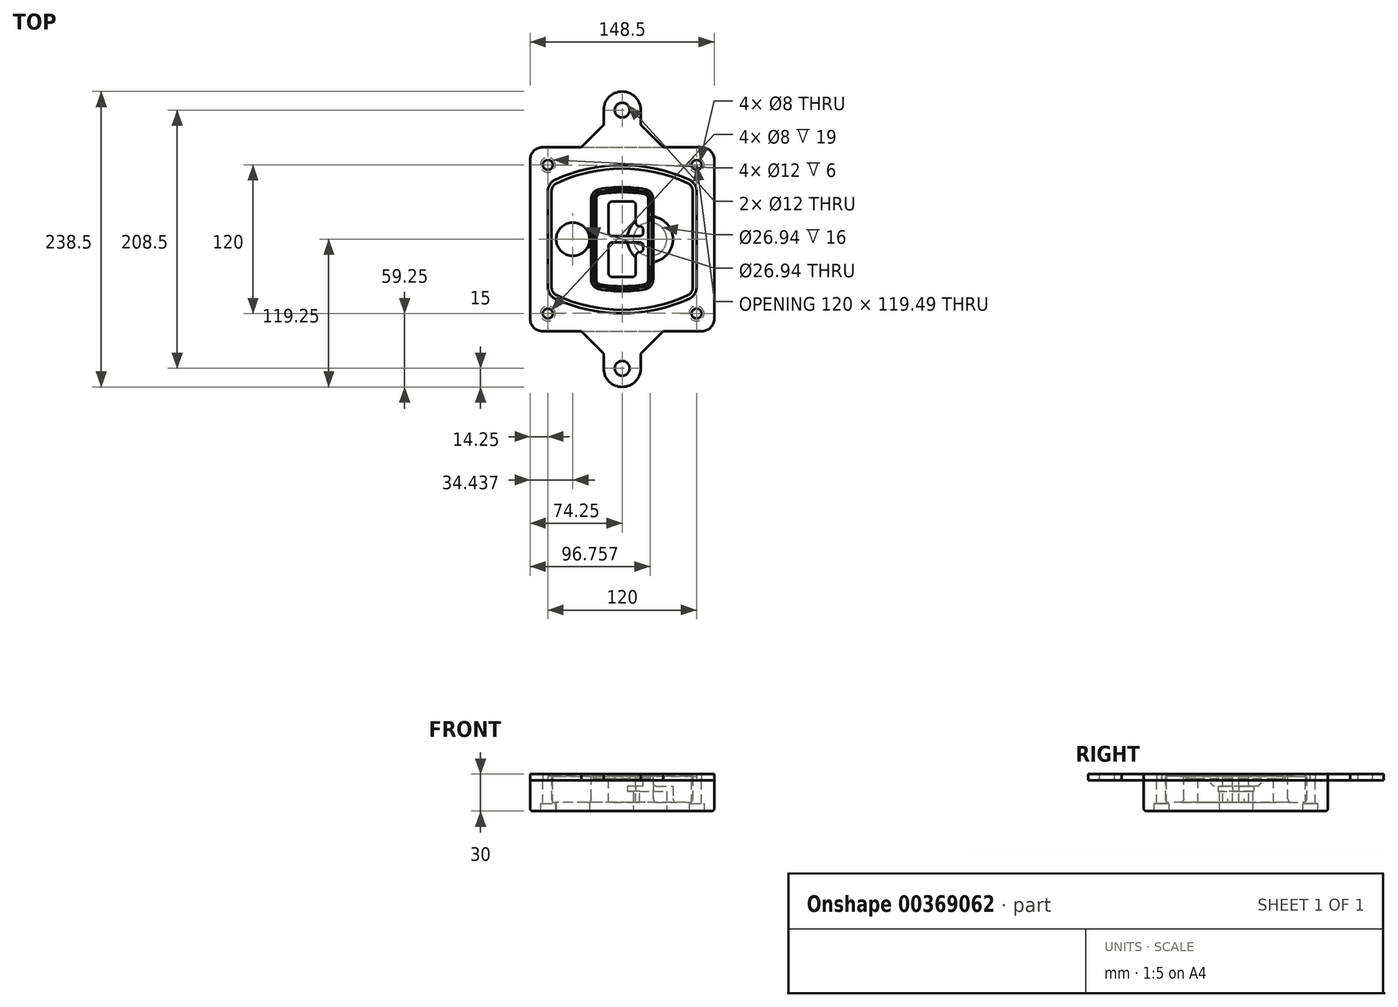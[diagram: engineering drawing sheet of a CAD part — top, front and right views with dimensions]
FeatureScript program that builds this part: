
annotation { "Feature Type Name" : "Feature", "Feature Type Description" : "" }
export const myFeature = defineFeature(function(context is Context, id is Id, definition is map)
    precondition{}
    {
        {
            var Q0;
            Q0=qCreatedBy(makeId("Top.planeOp"),FACE);
            var sketch = newSketch(context, id + "F0", { "sketchPlane" : qUnion([Q0])});
            skPoint(sketch, "E0.rect.middle", {"position": v(0, 0) * mm});
            skLineSegment(sketch, "E1.bottom", {"start": v(-64.25, -74.25) * mm, "end": v(64.25, -74.25) * mm});
            skLineSegment(sketch, "E1.top", {"start": v(-64.25, 74.25) * mm, "end": v(64.25, 74.25) * mm});
            skLineSegment(sketch, "E1.left", {"start": v(-74.25, -64.25) * mm, "end": v(-74.25, 64.25) * mm});
            skLineSegment(sketch, "E1.right", {"start": v(74.25, -64.25) * mm, "end": v(74.25, 64.25) * mm});
            skLineSegment(sketch, "E2", {"start": v(-74.25, 74.25) * mm, "end": v(74.25, -74.25) * mm, "construction": true});
            skLineSegment(sketch, "E3", {"start": v(74.25, 74.25) * mm, "end": v(-74.25, -74.25) * mm, "construction": true});
            skCircle(sketch, "E4", {"center": v(-60, 60) * mm, "radius": 4 * mm});
            skCircle(sketch, "E5", {"center": v(60, 60) * mm, "radius": 4 * mm});
            skCircle(sketch, "E6", {"center": v(60, -60) * mm, "radius": 4 * mm});
            skCircle(sketch, "E7", {"center": v(-60, -60) * mm, "radius": 4 * mm});
            skLineSegment(sketch, "E8", {"start": v(-60, 60) * mm, "end": v(60, 60) * mm, "construction": true});
            skLineSegment(sketch, "E9", {"start": v(60, 60) * mm, "end": v(60, -60) * mm, "construction": true});
            skLineSegment(sketch, "E10", {"start": v(60, -60) * mm, "end": v(-60, -60) * mm, "construction": true});
            skLineSegment(sketch, "E11", {"start": v(-60, -60) * mm, "end": v(-60, 60) * mm, "construction": true});
            skLineSegment(sketch, "E12", {"start": v(-60, 38.83) * mm, "end": v(-60, -38.83) * mm});
            skLineSegment(sketch, "E13", {"start": v(60, 38.83) * mm, "end": v(60, -38.83) * mm});
            skArc(sketch, "E14", {"start": v(54.26, 47.88) * mm, "mid": v(0, 60) * mm, "end": v(-54.26, 47.88) * mm});
            skArc(sketch, "E15", {"start": v(-54.26, -47.88) * mm, "mid": v(0, -60) * mm, "end": v(54.26, -47.88) * mm});
            skLineSegment(sketch, "E16", {"start": v(-60, 0) * mm, "end": v(60, 0) * mm, "construction": true});
            skPoint(sketch, "E17.visualSharp", {"position": v(-60, -45) * mm});
            skArc(sketch, "E17.filletArc", {"start": v(-60, -38.83) * mm, "mid": v(-58.44, -44.2) * mm, "end": v(-54.26, -47.88) * mm});
            skPoint(sketch, "E18.visualSharp", {"position": v(-60, 45) * mm});
            skArc(sketch, "E18.filletArc", {"start": v(-54.26, 47.88) * mm, "mid": v(-58.44, 44.2) * mm, "end": v(-60, 38.83) * mm});
            skPoint(sketch, "E19.visualSharp", {"position": v(60, 45) * mm});
            skArc(sketch, "E19.filletArc", {"start": v(60, 38.83) * mm, "mid": v(58.44, 44.2) * mm, "end": v(54.26, 47.88) * mm});
            skPoint(sketch, "E20.visualSharp", {"position": v(60, -45) * mm});
            skArc(sketch, "E20.filletArc", {"start": v(54.26, -47.88) * mm, "mid": v(58.44, -44.2) * mm, "end": v(60, -38.83) * mm});
            skPoint(sketch, "E21.visualSharp", {"position": v(-74.25, 74.25) * mm});
            skArc(sketch, "E21.filletArc", {"start": v(-64.25, 74.25) * mm, "mid": v(-71.32, 71.32) * mm, "end": v(-74.25, 64.25) * mm});
            skPoint(sketch, "E22.visualSharp", {"position": v(74.25, 74.25) * mm});
            skArc(sketch, "E22.filletArc", {"start": v(74.25, 64.25) * mm, "mid": v(71.32, 71.32) * mm, "end": v(64.25, 74.25) * mm});
            skPoint(sketch, "E23.visualSharp", {"position": v(74.25, -74.25) * mm});
            skArc(sketch, "E23.filletArc", {"start": v(64.25, -74.25) * mm, "mid": v(71.32, -71.32) * mm, "end": v(74.25, -64.25) * mm});
            skPoint(sketch, "E24.visualSharp", {"position": v(-74.25, -74.25) * mm});
            skArc(sketch, "E24.filletArc", {"start": v(-74.25, -64.25) * mm, "mid": v(-71.32, -71.32) * mm, "end": v(-64.25, -74.25) * mm});
            skArc(sketch, "E25.0", {"start": v(57, 38.83) * mm, "mid": v(55.9, 42.58) * mm, "end": v(52.98, 45.17) * mm});
            skLineSegment(sketch, "E25.1", {"start": v(57, 38.83) * mm, "end": v(57, -38.83) * mm});
            skArc(sketch, "E25.2", {"start": v(52.98, -45.17) * mm, "mid": v(55.9, -42.58) * mm, "end": v(57, -38.83) * mm});
            skArc(sketch, "E25.3", {"start": v(-52.98, -45.17) * mm, "mid": v(0, -57) * mm, "end": v(52.98, -45.17) * mm});
            skArc(sketch, "E25.4", {"start": v(-57, -38.83) * mm, "mid": v(-55.9, -42.58) * mm, "end": v(-52.98, -45.17) * mm});
            skArc(sketch, "E25.5", {"start": v(52.98, 45.17) * mm, "mid": v(0, 57) * mm, "end": v(-52.98, 45.17) * mm});
            skLineSegment(sketch, "E25.6", {"start": v(-57, 38.83) * mm, "end": v(-57, -38.83) * mm});
            skArc(sketch, "E25.7", {"start": v(-52.98, 45.17) * mm, "mid": v(-55.9, 42.58) * mm, "end": v(-57, 38.83) * mm});
            skArc(sketch, "E26.0", {"start": v(-55.96, 51.5) * mm, "mid": v(-61.82, 46.33) * mm, "end": v(-64, 38.83) * mm});
            skArc(sketch, "E26.1", {"start": v(55.96, 51.5) * mm, "mid": v(0, 64) * mm, "end": v(-55.96, 51.5) * mm});
            skArc(sketch, "E26.2", {"start": v(64, 38.83) * mm, "mid": v(61.82, 46.33) * mm, "end": v(55.96, 51.5) * mm});
            skLineSegment(sketch, "E26.3", {"start": v(64, 38.83) * mm, "end": v(64, -38.83) * mm});
            skArc(sketch, "E26.4", {"start": v(55.96, -51.5) * mm, "mid": v(61.82, -46.33) * mm, "end": v(64, -38.83) * mm});
            skLineSegment(sketch, "E26.5", {"start": v(-64, 38.83) * mm, "end": v(-64, -38.83) * mm});
            skArc(sketch, "E26.6", {"start": v(-55.96, -51.5) * mm, "mid": v(0, -64) * mm, "end": v(55.96, -51.5) * mm});
            skArc(sketch, "E26.7", {"start": v(-64, -38.83) * mm, "mid": v(-61.82, -46.33) * mm, "end": v(-55.96, -51.5) * mm});
            skSolve(sketch);
        }
        {
            var Q0;
            Q0=makeQuery(id+"F0.imprint","IMPRINT",FACE,{"disambiguationData":[TD([[makeQuery(id+"F0.imprint","IMPRINT",EDGE,{"derivedFrom":sQuery(id+"F0.wireOp",EDGE,"E1.bottom")}),1.0]])]});
            var Q1;
            Q1=makeQuery(id+"F0.imprint","IMPRINT",FACE,{"disambiguationData":[TD([[makeQuery(id+"F0.imprint","IMPRINT",EDGE,{"derivedFrom":sQuery(id+"F0.wireOp",EDGE,"E12")}),1.0]])]});
            var Q2;
            Q2=makeQuery(id+"F0.imprint","IMPRINT",FACE,{"disambiguationData":[TD([[makeQuery(id+"F0.imprint","IMPRINT",EDGE,{"derivedFrom":sQuery(id+"F0.wireOp",EDGE,"E25.0")}),1.0]])]});
            var Q3;
            Q3=makeQuery(id+"F0.imprint","IMPRINT",FACE,{"disambiguationData":[TD([[makeQuery(id+"F0.imprint","IMPRINT",EDGE,{"derivedFrom":sQuery(id+"F0.wireOp",EDGE,"E12")}),-1.0]])]});
            extrude(context, id + "F1", {"entities" : qUnion([Q0, Q1, Q2, Q3]), "oppositeDirection" : true, "depth" : 25 * mm});
        }
        {
            var Q0;
            Q0=makeQuery(id+"F0.imprint","IMPRINT",FACE,{"disambiguationData":[TD([[makeQuery(id+"F0.imprint","IMPRINT",EDGE,{"derivedFrom":sQuery(id+"F0.wireOp",EDGE,"E12")}),1.0]])]});
            extrude(context, id + "F2", {"entities" : qUnion([Q0]), "operationType" : NewBodyOperationType.ADD, "depth" : 3 * mm});
        }
        {
            var Q0;
            Q0=makeQuery(id+"F0.imprint","IMPRINT",FACE,{"disambiguationData":[TD([[makeQuery(id+"F0.imprint","IMPRINT",EDGE,{"derivedFrom":sQuery(id+"F0.wireOp",EDGE,"E25.0")}),1.0]])]});
            extrude(context, id + "F3", {"entities" : qUnion([Q0]), "operationType" : NewBodyOperationType.REMOVE, "oppositeDirection" : true, "depth" : 18 * mm});
        }
        {
            var Q0;
            Q0=makeQuery(id+"F2.opExtrude","CAP_FACE",FACE,{"disambiguationData":[OSD([sQuery(id+"F0.wireOp",EDGE,"E12"),sQuery(id+"F0.wireOp",EDGE,"E13"),sQuery(id+"F0.wireOp",EDGE,"E14"),sQuery(id+"F0.wireOp",EDGE,"E15"),sQuery(id+"F0.wireOp",EDGE,"E17.filletArc"),sQuery(id+"F0.wireOp",EDGE,"E18.filletArc"),sQuery(id+"F0.wireOp",EDGE,"E19.filletArc"),sQuery(id+"F0.wireOp",EDGE,"E20.filletArc"),sQuery(id+"F0.wireOp",EDGE,"E25.0"),sQuery(id+"F0.wireOp",EDGE,"E25.1"),sQuery(id+"F0.wireOp",EDGE,"E25.2"),sQuery(id+"F0.wireOp",EDGE,"E25.3"),sQuery(id+"F0.wireOp",EDGE,"E25.4"),sQuery(id+"F0.wireOp",EDGE,"E25.5"),sQuery(id+"F0.wireOp",EDGE,"E25.6"),sQuery(id+"F0.wireOp",EDGE,"E25.7")])],"isStart":false});
            var sketch = newSketch(context, id + "F4", { "sketchPlane" : qUnion([Q0])});
            skArc(sketch, "E27.0", {"start": v(-18.34, -40.45) * mm, "mid": v(0, -42) * mm, "end": v(18.34, -40.45) * mm});
            skArc(sketch, "E28.0", {"start": v(18.34, 40.45) * mm, "mid": v(0, 42) * mm, "end": v(-18.34, 40.45) * mm});
            skLineSegment(sketch, "E29", {"start": v(-25, 32.57) * mm, "end": v(-25, -32.57) * mm});
            skLineSegment(sketch, "E30", {"start": v(25, 32.57) * mm, "end": v(25, -32.57) * mm});
            skLineSegment(sketch, "E31", {"start": v(-25, 39.1) * mm, "end": v(25, 39.1) * mm, "construction": true});
            skLineSegment(sketch, "E32", {"start": v(-25, -39.1) * mm, "end": v(25, -39.1) * mm, "construction": true});
            skPoint(sketch, "E33.visualSharp", {"position": v(-25, 39.1) * mm});
            skArc(sketch, "E33.filletArc", {"start": v(-18.34, 40.45) * mm, "mid": v(-23.11, 37.73) * mm, "end": v(-25, 32.57) * mm});
            skPoint(sketch, "E34.visualSharp", {"position": v(25, 39.1) * mm});
            skArc(sketch, "E34.filletArc", {"start": v(25, 32.57) * mm, "mid": v(23.11, 37.73) * mm, "end": v(18.34, 40.45) * mm});
            skPoint(sketch, "E35.visualSharp", {"position": v(25, -39.1) * mm});
            skArc(sketch, "E35.filletArc", {"start": v(18.34, -40.45) * mm, "mid": v(23.11, -37.73) * mm, "end": v(25, -32.57) * mm});
            skPoint(sketch, "E36.visualSharp", {"position": v(-25, -39.1) * mm});
            skArc(sketch, "E36.filletArc", {"start": v(-25, -32.57) * mm, "mid": v(-23.11, -37.73) * mm, "end": v(-18.34, -40.45) * mm});
            skArc(sketch, "E37.0", {"start": v(52.98, 45.17) * mm, "mid": v(0, 57) * mm, "end": v(-52.98, 45.17) * mm});
            skArc(sketch, "E37.1", {"start": v(-52.98, 45.17) * mm, "mid": v(-55.9, 42.58) * mm, "end": v(-57, 38.83) * mm});
            skLineSegment(sketch, "E37.2", {"start": v(-57, 38.83) * mm, "end": v(-57, -38.83) * mm});
            skArc(sketch, "E37.3", {"start": v(-57, -38.83) * mm, "mid": v(-55.9, -42.58) * mm, "end": v(-52.98, -45.17) * mm});
            skArc(sketch, "E37.4", {"start": v(-52.98, -45.17) * mm, "mid": v(0, -57) * mm, "end": v(52.98, -45.17) * mm});
            skArc(sketch, "E37.5", {"start": v(52.98, -45.17) * mm, "mid": v(55.9, -42.58) * mm, "end": v(57, -38.83) * mm});
            skLineSegment(sketch, "E37.6", {"start": v(57, 38.83) * mm, "end": v(57, -38.83) * mm});
            skArc(sketch, "E37.7", {"start": v(57, 38.83) * mm, "mid": v(55.9, 42.58) * mm, "end": v(52.98, 45.17) * mm});
            skLineSegment(sketch, "E38.0", {"start": v(23, 32.57) * mm, "end": v(23, -32.57) * mm});
            skArc(sketch, "E38.1", {"start": v(18, -38.48) * mm, "mid": v(21.58, -36.44) * mm, "end": v(23, -32.57) * mm});
            skArc(sketch, "E38.2", {"start": v(-18, -38.48) * mm, "mid": v(0, -40) * mm, "end": v(18, -38.48) * mm});
            skArc(sketch, "E38.3", {"start": v(-23, -32.57) * mm, "mid": v(-21.58, -36.44) * mm, "end": v(-18, -38.48) * mm});
            skLineSegment(sketch, "E38.4", {"start": v(-23, 32.57) * mm, "end": v(-23, -32.57) * mm});
            skArc(sketch, "E38.5", {"start": v(23, 32.57) * mm, "mid": v(21.58, 36.44) * mm, "end": v(18, 38.48) * mm});
            skArc(sketch, "E38.6", {"start": v(-18, 38.48) * mm, "mid": v(-21.58, 36.44) * mm, "end": v(-23, 32.57) * mm});
            skArc(sketch, "E38.7", {"start": v(18, 38.48) * mm, "mid": v(0, 40) * mm, "end": v(-18, 38.48) * mm});
            skArc(sketch, "E39.0", {"start": v(21, 32.57) * mm, "mid": v(20.06, 35.15) * mm, "end": v(17.67, 36.5) * mm});
            skLineSegment(sketch, "E39.1", {"start": v(21, 32.57) * mm, "end": v(21, -32.57) * mm});
            skArc(sketch, "E39.2", {"start": v(17.67, -36.5) * mm, "mid": v(20.06, -35.15) * mm, "end": v(21, -32.57) * mm});
            skArc(sketch, "E39.3", {"start": v(-17.67, -36.5) * mm, "mid": v(0, -38) * mm, "end": v(17.67, -36.5) * mm});
            skArc(sketch, "E39.4", {"start": v(-21, -32.57) * mm, "mid": v(-20.06, -35.15) * mm, "end": v(-17.67, -36.5) * mm});
            skArc(sketch, "E39.5", {"start": v(17.67, 36.5) * mm, "mid": v(0, 38) * mm, "end": v(-17.67, 36.5) * mm});
            skLineSegment(sketch, "E39.6", {"start": v(-21, 32.57) * mm, "end": v(-21, -32.57) * mm});
            skArc(sketch, "E39.7", {"start": v(-17.67, 36.5) * mm, "mid": v(-20.06, 35.15) * mm, "end": v(-21, 32.57) * mm});
            skLineSegment(sketch, "E40", {"start": v(-25, 0) * mm, "end": v(25, 0) * mm, "construction": true});
            skLineSegment(sketch, "E41", {"start": v(-11, 5.5) * mm, "end": v(-11, 27.5) * mm});
            skLineSegment(sketch, "E42", {"start": v(-8, 30.5) * mm, "end": v(8, 30.5) * mm});
            skLineSegment(sketch, "E43", {"start": v(11, 27.5) * mm, "end": v(11, 13.5) * mm});
            skLineSegment(sketch, "E44", {"start": v(14, 10.5) * mm, "end": v(14, 10.5) * mm});
            skLineSegment(sketch, "E45", {"start": v(17, 7.5) * mm, "end": v(17, 5.5) * mm});
            skLineSegment(sketch, "E46", {"start": v(14, 2.5) * mm, "end": v(-8, 2.5) * mm});
            skPoint(sketch, "E47.visualSharp", {"position": v(-11, 30.5) * mm});
            skArc(sketch, "E47.filletArc", {"start": v(-8, 30.5) * mm, "mid": v(-10.12, 29.62) * mm, "end": v(-11, 27.5) * mm});
            skPoint(sketch, "E48.visualSharp", {"position": v(11, 30.5) * mm});
            skArc(sketch, "E48.filletArc", {"start": v(11, 27.5) * mm, "mid": v(10.12, 29.62) * mm, "end": v(8, 30.5) * mm});
            skPoint(sketch, "E49.visualSharp", {"position": v(11, 10.5) * mm});
            skArc(sketch, "E49.filletArc", {"start": v(11, 13.5) * mm, "mid": v(11.88, 11.38) * mm, "end": v(14, 10.5) * mm});
            skPoint(sketch, "E50.visualSharp", {"position": v(17, 10.5) * mm});
            skArc(sketch, "E50.filletArc", {"start": v(17, 7.5) * mm, "mid": v(16.12, 9.62) * mm, "end": v(14, 10.5) * mm});
            skPoint(sketch, "E51.visualSharp", {"position": v(17, 2.5) * mm});
            skArc(sketch, "E51.filletArc", {"start": v(14, 2.5) * mm, "mid": v(16.12, 3.38) * mm, "end": v(17, 5.5) * mm});
            skPoint(sketch, "E52.visualSharp", {"position": v(-11, 2.5) * mm});
            skArc(sketch, "E52.filletArc", {"start": v(-11, 5.5) * mm, "mid": v(-10.12, 3.38) * mm, "end": v(-8, 2.5) * mm});
            skLineSegment(sketch, "E53.0.MirrorCS", {"start": v(14, -2.5) * mm, "end": v(-8, -2.5) * mm});
            skArc(sketch, "E54.0.MirrorCS", {"start": v(-11, -5.5) * mm, "mid": v(-10.12, -3.38) * mm, "end": v(-8, -2.5) * mm});
            skLineSegment(sketch, "E55.0.MirrorCS", {"start": v(-11, -5.5) * mm, "end": v(-11, -27.5) * mm});
            skArc(sketch, "E56.0.MirrorCS", {"start": v(-8, -30.5) * mm, "mid": v(-10.12, -29.62) * mm, "end": v(-11, -27.5) * mm});
            skLineSegment(sketch, "E57.0.MirrorCS", {"start": v(-8, -30.5) * mm, "end": v(8, -30.5) * mm});
            skArc(sketch, "E58.0.MirrorCS", {"start": v(11, -27.5) * mm, "mid": v(10.12, -29.62) * mm, "end": v(8, -30.5) * mm});
            skLineSegment(sketch, "E59.0.MirrorCS", {"start": v(11, -27.5) * mm, "end": v(11, -13.5) * mm});
            skArc(sketch, "E60.0.MirrorCS", {"start": v(11, -13.5) * mm, "mid": v(11.88, -11.38) * mm, "end": v(14, -10.5) * mm});
            skArc(sketch, "E61.0.MirrorCS", {"start": v(17, -7.5) * mm, "mid": v(16.12, -9.62) * mm, "end": v(14, -10.5) * mm});
            skLineSegment(sketch, "E62.0.MirrorCS", {"start": v(17, -7.5) * mm, "end": v(17, -5.5) * mm});
            skArc(sketch, "E63.0.MirrorCS", {"start": v(14, -2.5) * mm, "mid": v(16.12, -3.38) * mm, "end": v(17, -5.5) * mm});
            skSolve(sketch);
        }
        {
            var Q0;
            Q0=makeQuery(id+"F4.imprint","IMPRINT",FACE,{"disambiguationData":[TD([[makeQuery(id+"F4.imprint","IMPRINT",EDGE,{"derivedFrom":sQuery(id+"F4.wireOp",EDGE,"E27.0")}),1.0]])]});
            var Q1;
            Q1=makeQuery(id+"F4.imprint","IMPRINT",FACE,{"disambiguationData":[TD([[makeQuery(id+"F4.imprint","IMPRINT",EDGE,{"derivedFrom":sQuery(id+"F4.wireOp",EDGE,"E38.0")}),-1.0]])]});
            var Q2;
            Q2=makeQuery(id+"F4.imprint","IMPRINT",FACE,{"disambiguationData":[TD([[makeQuery(id+"F4.imprint","IMPRINT",EDGE,{"derivedFrom":sQuery(id+"F4.wireOp",EDGE,"E39.0")}),1.0]])]});
            extrude(context, id + "F5", {"entities" : qUnion([Q0, Q1, Q2]), "operationType" : NewBodyOperationType.ADD, "endBound" : BoundingType.UP_TO_NEXT, "oppositeDirection" : true, "depth" : 25 * mm});
        }
        {
            var Q0;
            Q0=makeQuery(id+"F4.imprint","IMPRINT",FACE,{"disambiguationData":[TD([[makeQuery(id+"F4.imprint","IMPRINT",EDGE,{"derivedFrom":sQuery(id+"F4.wireOp",EDGE,"E38.0")}),-1.0]])]});
            extrude(context, id + "F6", {"entities" : qUnion([Q0]), "operationType" : NewBodyOperationType.REMOVE, "oppositeDirection" : true, "depth" : 2 * mm});
        }
        {
            var Q0;
            Q0=makeQuery(id+"F1.opExtrude","CAP_FACE",FACE,{"disambiguationData":[OSD([sQuery(id+"F0.wireOp",EDGE,"E1.bottom"),sQuery(id+"F0.wireOp",EDGE,"E1.top"),sQuery(id+"F0.wireOp",EDGE,"E1.left"),sQuery(id+"F0.wireOp",EDGE,"E1.right"),sQuery(id+"F0.wireOp",EDGE,"E4"),sQuery(id+"F0.wireOp",EDGE,"E5"),sQuery(id+"F0.wireOp",EDGE,"E6"),sQuery(id+"F0.wireOp",EDGE,"E7"),sQuery(id+"F0.wireOp",EDGE,"E21.filletArc"),sQuery(id+"F0.wireOp",EDGE,"E22.filletArc"),sQuery(id+"F0.wireOp",EDGE,"E23.filletArc"),sQuery(id+"F0.wireOp",EDGE,"E24.filletArc")])],"isStart":false});
            var sketch = newSketch(context, id + "F7", { "sketchPlane" : qUnion([Q0])});
            skCircle(sketch, "E64", {"center": v(22.5, 0) * mm, "radius": 13.47 * mm});
            skCircle(sketch, "E65", {"center": v(-39.81, 0) * mm, "radius": 13.47 * mm});
            skLineSegment(sketch, "E66", {"start": v(74.25, 0) * mm, "end": v(-74.25, 0) * mm});
            skCircle(sketch, "E67", {"center": v(22.5, 0) * mm, "radius": 18.47 * mm});
            skCircle(sketch, "E68", {"center": v(60, -60) * mm, "radius": 6 * mm});
            skCircle(sketch, "E69", {"center": v(-60, -60) * mm, "radius": 6 * mm});
            skCircle(sketch, "E70", {"center": v(-60, 60) * mm, "radius": 6 * mm});
            skCircle(sketch, "E71", {"center": v(60, 60) * mm, "radius": 6 * mm});
            skSolve(sketch);
        }
        {
            var Q0;
            {var subQ1=sQuery(id+"F7.wireOp",EDGE,"E66");var subQ4=sQuery(id+"F7.wireOp",EDGE,"E64");var subQ6=makeQuery(id+"F7.imprint","INTERSECT",VERTEX,{"disambiguationData":[OD(0.0)],"derivedFrom":[subQ4,subQ1]});Q0=makeQuery(id+"F7.imprint","IMPRINT",FACE,{"disambiguationData":[TD([[makeQuery(id+"F7.imprint","IMPRINT",EDGE,{"disambiguationData":[TD([[subQ6,-1.0]])],"derivedFrom":subQ4}),-1.0]])]});}
            var Q1;
            {var subQ0=sQuery(id+"F7.wireOp",EDGE,"E66");var subQ1=sQuery(id+"F7.wireOp",EDGE,"E64");var subQ3=makeQuery(id+"F7.imprint","INTERSECT",VERTEX,{"disambiguationData":[OD(0.0)],"derivedFrom":[subQ1,subQ0]});Q1=makeQuery(id+"F7.imprint","IMPRINT",FACE,{"disambiguationData":[TD([[makeQuery(id+"F7.imprint","IMPRINT",EDGE,{"disambiguationData":[TD([[subQ3,-1.0]])],"derivedFrom":subQ1}),1.0]])]});}
            var Q2;
            {var subQ0=sQuery(id+"F7.wireOp",EDGE,"E66");var subQ1=sQuery(id+"F7.wireOp",EDGE,"E64");var subQ3=makeQuery(id+"F7.imprint","INTERSECT",VERTEX,{"disambiguationData":[OD(0.0)],"derivedFrom":[subQ1,subQ0]});Q2=makeQuery(id+"F7.imprint","IMPRINT",FACE,{"disambiguationData":[TD([[makeQuery(id+"F7.imprint","IMPRINT",EDGE,{"disambiguationData":[TD([[subQ3,1.0]])],"derivedFrom":subQ1}),1.0]])]});}
            var Q3;
            {var subQ1=sQuery(id+"F7.wireOp",EDGE,"E66");var subQ4=sQuery(id+"F7.wireOp",EDGE,"E64");var subQ6=makeQuery(id+"F7.imprint","INTERSECT",VERTEX,{"disambiguationData":[OD(0.0)],"derivedFrom":[subQ4,subQ1]});Q3=makeQuery(id+"F7.imprint","IMPRINT",FACE,{"disambiguationData":[TD([[makeQuery(id+"F7.imprint","IMPRINT",EDGE,{"disambiguationData":[TD([[subQ6,1.0]])],"derivedFrom":subQ4}),-1.0]])]});}
            extrude(context, id + "F8", {"entities" : qUnion([Q0, Q1, Q2, Q3]), "operationType" : NewBodyOperationType.ADD, "oppositeDirection" : true, "depth" : 20 * mm});
        }
        {
            var Q0;
            {var subQ0=sQuery(id+"F7.wireOp",EDGE,"E66");var subQ1=sQuery(id+"F7.wireOp",EDGE,"E64");var subQ3=makeQuery(id+"F7.imprint","INTERSECT",VERTEX,{"disambiguationData":[OD(0.0)],"derivedFrom":[subQ1,subQ0]});Q0=makeQuery(id+"F7.imprint","IMPRINT",FACE,{"disambiguationData":[TD([[makeQuery(id+"F7.imprint","IMPRINT",EDGE,{"disambiguationData":[TD([[subQ3,-1.0]])],"derivedFrom":subQ1}),1.0]])]});}
            var Q1;
            {var subQ0=sQuery(id+"F7.wireOp",EDGE,"E66");var subQ1=sQuery(id+"F7.wireOp",EDGE,"E64");var subQ3=makeQuery(id+"F7.imprint","INTERSECT",VERTEX,{"disambiguationData":[OD(0.0)],"derivedFrom":[subQ1,subQ0]});Q1=makeQuery(id+"F7.imprint","IMPRINT",FACE,{"disambiguationData":[TD([[makeQuery(id+"F7.imprint","IMPRINT",EDGE,{"disambiguationData":[TD([[subQ3,1.0]])],"derivedFrom":subQ1}),1.0]])]});}
            extrude(context, id + "F9", {"entities" : qUnion([Q0, Q1]), "operationType" : NewBodyOperationType.REMOVE, "oppositeDirection" : true, "depth" : 16 * mm});
        }
        {
            var Q0;
            {var subQ0=sQuery(id+"F7.wireOp",EDGE,"E66");var subQ1=sQuery(id+"F7.wireOp",EDGE,"E65");var subQ3=makeQuery(id+"F7.imprint","INTERSECT",VERTEX,{"disambiguationData":[OD(0.0)],"derivedFrom":[subQ1,subQ0]});Q0=makeQuery(id+"F7.imprint","IMPRINT",FACE,{"disambiguationData":[TD([[makeQuery(id+"F7.imprint","IMPRINT",EDGE,{"disambiguationData":[TD([[subQ3,-1.0]])],"derivedFrom":subQ1}),1.0]])]});}
            var Q1;
            {var subQ0=sQuery(id+"F7.wireOp",EDGE,"E66");var subQ1=sQuery(id+"F7.wireOp",EDGE,"E65");var subQ3=makeQuery(id+"F7.imprint","INTERSECT",VERTEX,{"disambiguationData":[OD(0.0)],"derivedFrom":[subQ1,subQ0]});Q1=makeQuery(id+"F7.imprint","IMPRINT",FACE,{"disambiguationData":[TD([[makeQuery(id+"F7.imprint","IMPRINT",EDGE,{"disambiguationData":[TD([[subQ3,1.0]])],"derivedFrom":subQ1}),1.0]])]});}
            extrude(context, id + "F10", {"entities" : qUnion([Q0, Q1]), "operationType" : NewBodyOperationType.REMOVE, "oppositeDirection" : true, "depth" : 25 * mm});
        }
        {
            var Q0;
            Q0=makeQuery(id+"F7.imprint","IMPRINT",FACE,{"disambiguationData":[TD([[makeQuery(id+"F7.imprint","IMPRINT",EDGE,{"derivedFrom":sQuery(id+"F7.wireOp",EDGE,"E68")}),1.0]])]});
            var Q1;
            Q1=makeQuery(id+"F7.imprint","IMPRINT",FACE,{"disambiguationData":[TD([[makeQuery(id+"F7.imprint","IMPRINT",EDGE,{"derivedFrom":makeQuery(id+"F1.opExtrude","CAP_EDGE",EDGE,{"disambiguationData":[OSD([sQuery(id+"F0.wireOp",EDGE,"E5")])],"isStart":false})}),-1.0]])]});
            var Q2;
            Q2=makeQuery(id+"F7.imprint","IMPRINT",FACE,{"disambiguationData":[TD([[makeQuery(id+"F7.imprint","IMPRINT",EDGE,{"derivedFrom":sQuery(id+"F7.wireOp",EDGE,"E69")}),1.0]])]});
            var Q3;
            Q3=makeQuery(id+"F7.imprint","IMPRINT",FACE,{"disambiguationData":[TD([[makeQuery(id+"F7.imprint","IMPRINT",EDGE,{"derivedFrom":makeQuery(id+"F1.opExtrude","CAP_EDGE",EDGE,{"disambiguationData":[OSD([sQuery(id+"F0.wireOp",EDGE,"E4")])],"isStart":false})}),-1.0]])]});
            var Q4;
            Q4=makeQuery(id+"F7.imprint","IMPRINT",FACE,{"disambiguationData":[TD([[makeQuery(id+"F7.imprint","IMPRINT",EDGE,{"derivedFrom":sQuery(id+"F7.wireOp",EDGE,"E70")}),1.0]])]});
            var Q5;
            Q5=makeQuery(id+"F7.imprint","IMPRINT",FACE,{"disambiguationData":[TD([[makeQuery(id+"F7.imprint","IMPRINT",EDGE,{"derivedFrom":makeQuery(id+"F1.opExtrude","CAP_EDGE",EDGE,{"disambiguationData":[OSD([sQuery(id+"F0.wireOp",EDGE,"E7")])],"isStart":false})}),-1.0]])]});
            var Q6;
            Q6=makeQuery(id+"F7.imprint","IMPRINT",FACE,{"disambiguationData":[TD([[makeQuery(id+"F7.imprint","IMPRINT",EDGE,{"derivedFrom":sQuery(id+"F7.wireOp",EDGE,"E71")}),1.0]])]});
            var Q7;
            Q7=makeQuery(id+"F7.imprint","IMPRINT",FACE,{"disambiguationData":[TD([[makeQuery(id+"F7.imprint","IMPRINT",EDGE,{"derivedFrom":makeQuery(id+"F1.opExtrude","CAP_EDGE",EDGE,{"disambiguationData":[OSD([sQuery(id+"F0.wireOp",EDGE,"E6")])],"isStart":false})}),-1.0]])]});
            extrude(context, id + "F11", {"entities" : qUnion([Q0, Q1, Q2, Q3, Q4, Q5, Q6, Q7]), "operationType" : NewBodyOperationType.REMOVE, "oppositeDirection" : true, "depth" : 6 * mm});
        }
        {
            var Q0;
            Q0=makeQuery(id+"F9.boolean.opBoolean","COPY",FACE,{"derivedFrom":makeQuery(id+"F9.opExtrude","CAP_FACE",FACE,{"disambiguationData":[OSD([sQuery(id+"F7.wireOp",EDGE,"E64")])],"isStart":false})});
            var sketch = newSketch(context, id + "F12", { "sketchPlane" : qUnion([Q0])});
            skArc(sketch, "E72.0", {"start": v(11, 14.45) * mm, "mid": v(6.45, 9.13) * mm, "end": v(4.2, 2.5) * mm});
            skArc(sketch, "E72.1", {"start": v(4.2, -2.5) * mm, "mid": v(6.45, -9.13) * mm, "end": v(11, -14.45) * mm});
            skLineSegment(sketch, "E73", {"start": v(4.2, -2.5) * mm, "end": v(14, -2.5) * mm});
            skLineSegment(sketch, "E74.0", {"start": v(14, 2.5) * mm, "end": v(4.2, 2.5) * mm});
            skArc(sketch, "E74.1", {"start": v(14, 2.5) * mm, "mid": v(16.12, 3.38) * mm, "end": v(17, 5.5) * mm});
            skLineSegment(sketch, "E74.2", {"start": v(17, 7.5) * mm, "end": v(17, 5.5) * mm});
            skArc(sketch, "E74.3", {"start": v(17, 7.5) * mm, "mid": v(16.12, 9.62) * mm, "end": v(14, 10.5) * mm});
            skArc(sketch, "E74.4", {"start": v(11, 13.5) * mm, "mid": v(11.88, 11.38) * mm, "end": v(14, 10.5) * mm});
            skLineSegment(sketch, "E74.5", {"start": v(11, 14.45) * mm, "end": v(11, 13.5) * mm});
            skLineSegment(sketch, "E74.7", {"start": v(14, -2.5) * mm, "end": v(4.2, -2.5) * mm});
            skArc(sketch, "E74.8", {"start": v(14, -2.5) * mm, "mid": v(16.12, -3.38) * mm, "end": v(17, -5.5) * mm});
            skLineSegment(sketch, "E74.9", {"start": v(17, -7.5) * mm, "end": v(17, -5.5) * mm});
            skArc(sketch, "E74.10", {"start": v(17, -7.5) * mm, "mid": v(16.12, -9.62) * mm, "end": v(14, -10.5) * mm});
            skArc(sketch, "E74.11", {"start": v(11, -13.5) * mm, "mid": v(11.88, -11.38) * mm, "end": v(14, -10.5) * mm});
            skLineSegment(sketch, "E74.12", {"start": v(11, -14.45) * mm, "end": v(11, -13.5) * mm});
            skPoint(sketch, "E75.orphan", {"position": v(11, -27.5) * mm});
            skPoint(sketch, "E76.orphan", {"position": v(-8, -2.5) * mm});
            skPoint(sketch, "E77.orphan", {"position": v(-8, 2.5) * mm});
            skPoint(sketch, "E78.orphan", {"position": v(11, 27.5) * mm});
            skSolve(sketch);
        }
        {
            var Q0;
            {var subQ7=sQuery(id+"F12.wireOp",EDGE,"E72.0");var subQ14=sQuery(id+"F12.wireOp",EDGE,"E72.1");var subQ16=sQuery(id+"F12.wireOp",EDGE,"E74.1");var subQ18=sQuery(id+"F12.wireOp",EDGE,"E74.8");Q0=qUnion([makeQuery(id+"F12.imprint","IMPRINT",FACE,{"disambiguationData":[TD([[makeQuery(id+"F12.imprint","IMPRINT",EDGE,{"derivedFrom":subQ7}),1.0]])]}),makeQuery(id+"F12.imprint","IMPRINT",FACE,{"disambiguationData":[TD([[makeQuery(id+"F12.imprint","IMPRINT",EDGE,{"derivedFrom":subQ14}),1.0]])]}),makeQuery(id+"F12.imprint","IMPRINT",FACE,{"disambiguationData":[TD([[makeQuery(id+"F12.imprint","IMPRINT",EDGE,{"derivedFrom":subQ16}),1.0]])]}),makeQuery(id+"F12.imprint","IMPRINT",FACE,{"disambiguationData":[TD([[makeQuery(id+"F12.imprint","IMPRINT",EDGE,{"derivedFrom":subQ18}),-1.0]])]})]);}
            var Q1;
            Q1=makeQuery(id+"F5.boolean.opBoolean","SPLIT",FACE,{"disambiguationData":[TD([makeQuery(id+"F5.opExtrude","SWEPT_FACE",FACE,{"disambiguationData":[OSD([sQuery(id+"F4.wireOp",EDGE,"E41")])]})])],"derivedFrom":makeQuery(id+"F3.boolean.opBoolean","COPY",FACE,{"derivedFrom":makeQuery(id+"F3.opExtrude","CAP_FACE",FACE,{"disambiguationData":[OSD([sQuery(id+"F0.wireOp",EDGE,"E25.0"),sQuery(id+"F0.wireOp",EDGE,"E25.1"),sQuery(id+"F0.wireOp",EDGE,"E25.2"),sQuery(id+"F0.wireOp",EDGE,"E25.3"),sQuery(id+"F0.wireOp",EDGE,"E25.4"),sQuery(id+"F0.wireOp",EDGE,"E25.5"),sQuery(id+"F0.wireOp",EDGE,"E25.6"),sQuery(id+"F0.wireOp",EDGE,"E25.7")])],"isStart":false})})});
            extrude(context, id + "F13", {"entities" : qUnion([Q0]), "operationType" : NewBodyOperationType.REMOVE, "endBound" : BoundingType.UP_TO_SURFACE, "endBoundEntityFace" : qUnion([Q1]), "depth" : 25 * mm});
        }
        {
            var Q0;
            Q0=makeQuery(id+"F3.boolean.opBoolean","COPY",EDGE,{"derivedFrom":makeQuery(id+"F3.opExtrude","CAP_EDGE",EDGE,{"disambiguationData":[OSD([sQuery(id+"F0.wireOp",EDGE,"E25.6")])],"isStart":false})});
            var Q1;
            Q1=makeQuery(id+"F8.boolean.opBoolean","INTERSECT",EDGE,{"derivedFrom":[makeQuery(id+"F5.opExtrude","SWEPT_FACE",FACE,{"disambiguationData":[OSD([sQuery(id+"F4.wireOp",EDGE,"E30")])]}),makeQuery(id+"F8.opExtrude","CAP_FACE",FACE,{"disambiguationData":[OSD([sQuery(id+"F7.wireOp",EDGE,"E67")])],"isStart":false})]});
            var Q2;
            Q2=makeQuery(id+"F8.boolean.opBoolean","INTERSECT",EDGE,{"disambiguationData":[OD(1.0)],"derivedFrom":[makeQuery(id+"F5.opExtrude","SWEPT_FACE",FACE,{"disambiguationData":[OSD([sQuery(id+"F4.wireOp",EDGE,"E30")])]}),makeQuery(id+"F8.opExtrude","SWEPT_FACE",FACE,{"disambiguationData":[OSD([sQuery(id+"F7.wireOp",EDGE,"E67")])]})]});
            var Q3;
            {var subQ0=sQuery(id+"F4.wireOp",EDGE,"E30");Q3=makeQuery(id+"F8.boolean.opBoolean","SPLIT",EDGE,{"disambiguationData":[TD([makeQuery(id+"F5.opExtrude","SWEPT_FACE",FACE,{"disambiguationData":[OSD([sQuery(id+"F4.wireOp",EDGE,"E35.filletArc")])]})])],"derivedFrom":makeQuery(id+"F5.opExtrude","CAP_EDGE",EDGE,{"disambiguationData":[OSD([subQ0])],"isStart":false})});}
            var Q4;
            {var subQ0=sQuery(id+"F0.wireOp",EDGE,"E25.7");var subQ1=sQuery(id+"F0.wireOp",EDGE,"E25.1");var subQ2=sQuery(id+"F0.wireOp",EDGE,"E25.6");var subQ3=sQuery(id+"F0.wireOp",EDGE,"E25.5");var subQ4=sQuery(id+"F0.wireOp",EDGE,"E25.4");var subQ5=sQuery(id+"F0.wireOp",EDGE,"E25.0");var subQ6=sQuery(id+"F0.wireOp",EDGE,"E25.2");var subQ7=sQuery(id+"F0.wireOp",EDGE,"E25.3");Q4=makeQuery(id+"F8.boolean.opBoolean","INTERSECT",EDGE,{"derivedFrom":[makeQuery(id+"F5.boolean.opBoolean","SPLIT",FACE,{"disambiguationData":[TD([makeQuery(id+"F2.opExtrude","SWEPT_FACE",FACE,{"disambiguationData":[OSD([subQ5])]})])],"derivedFrom":makeQuery(id+"F3.boolean.opBoolean","COPY",FACE,{"derivedFrom":makeQuery(id+"F3.opExtrude","CAP_FACE",FACE,{"disambiguationData":[OSD([subQ5,subQ1,subQ6,subQ7,subQ4,subQ3,subQ2,subQ0])],"isStart":false})})}),makeQuery(id+"F8.opExtrude","SWEPT_FACE",FACE,{"disambiguationData":[OSD([sQuery(id+"F7.wireOp",EDGE,"E67")])]})]});}
            var Q5;
            Q5=makeQuery(id+"F8.boolean.opBoolean","INTERSECT",EDGE,{"disambiguationData":[OD(0.0)],"derivedFrom":[makeQuery(id+"F5.opExtrude","SWEPT_FACE",FACE,{"disambiguationData":[OSD([sQuery(id+"F4.wireOp",EDGE,"E30")])]}),makeQuery(id+"F8.opExtrude","SWEPT_FACE",FACE,{"disambiguationData":[OSD([sQuery(id+"F7.wireOp",EDGE,"E67")])]})]});
            fillet(context, id + "F14", {"entities" : qUnion([Q0, Q1, Q2, Q3, Q4, Q5]), "radius" : 3 * mm, "tangentPropagation" : true, "allowEdgeOverflow" : false});
        }
        {
            var Q0;
            Q0=makeQuery(id+"F1.opExtrude","CAP_EDGE",EDGE,{"disambiguationData":[OSD([sQuery(id+"F0.wireOp",EDGE,"E1.bottom")])],"isStart":false});
            fillet(context, id + "F15", {"entities" : qUnion([Q0]), "radius" : 2 * mm, "tangentPropagation" : true, "allowEdgeOverflow" : false});
        }
        {
            var Q0;
            {var subQ0=sQuery(id+"F0.wireOp",EDGE,"E21.filletArc");var subQ1=sQuery(id+"F0.wireOp",EDGE,"E7");var subQ2=sQuery(id+"F0.wireOp",EDGE,"E6");var subQ3=sQuery(id+"F0.wireOp",EDGE,"E5");var subQ4=sQuery(id+"F0.wireOp",EDGE,"E4");var subQ5=sQuery(id+"F0.wireOp",EDGE,"E22.filletArc");var subQ6=sQuery(id+"F0.wireOp",EDGE,"E1.bottom");var subQ7=sQuery(id+"F0.wireOp",EDGE,"E1.right");var subQ8=sQuery(id+"F0.wireOp",EDGE,"E1.top");var subQ9=sQuery(id+"F0.wireOp",EDGE,"E1.left");var subQ10=sQuery(id+"F0.wireOp",EDGE,"E23.filletArc");var subQ11=sQuery(id+"F0.wireOp",EDGE,"E24.filletArc");Q0=makeQuery(id+"F2.boolean.opBoolean","SPLIT",FACE,{"disambiguationData":[TD([makeQuery(id+"F1.opExtrude","SWEPT_FACE",FACE,{"disambiguationData":[OSD([subQ6])]})])],"derivedFrom":makeQuery(id+"F1.opExtrude","CAP_FACE",FACE,{"disambiguationData":[OSD([subQ6,subQ8,subQ9,subQ7,subQ4,subQ3,subQ2,subQ1,subQ0,subQ5,subQ10,subQ11])],"isStart":true})});}
            var sketch = newSketch(context, id + "F16", { "sketchPlane" : qUnion([Q0])});
            skLineSegment(sketch, "E79", {"start": v(0, 74.25) * mm, "end": v(0, 104.25) * mm, "construction": true});
            skCircle(sketch, "E80", {"center": v(0, 104.25) * mm, "radius": 6 * mm});
            skArc(sketch, "E81", {"start": v(15, 104.25) * mm, "mid": v(0, 119.25) * mm, "end": v(-15, 104.25) * mm});
            skLineSegment(sketch, "E82", {"start": v(-15, 104.25) * mm, "end": v(-15, 92.25) * mm});
            skLineSegment(sketch, "E83", {"start": v(15, 104.25) * mm, "end": v(15, 92.25) * mm});
            skLineSegment(sketch, "E84", {"start": v(15, 92.25) * mm, "end": v(33, 74.25) * mm});
            skLineSegment(sketch, "E85.MirrorCS", {"start": v(-15, 92.25) * mm, "end": v(-33, 74.25) * mm});
            skPoint(sketch, "E86.endSnap0", {"position": v(-74.25, 0) * mm});
            skLineSegment(sketch, "E87.MirrorCS", {"start": v(15, -92.25) * mm, "end": v(33, -74.25) * mm});
            skLineSegment(sketch, "E88.MirrorCS", {"start": v(15, -104.25) * mm, "end": v(15, -92.25) * mm});
            skArc(sketch, "E89.MirrorCS", {"start": v(15, -104.25) * mm, "mid": v(0, -119.25) * mm, "end": v(-15, -104.25) * mm});
            skCircle(sketch, "E90.MirrorC", {"center": v(0, -104.25) * mm, "radius": 6 * mm});
            skLineSegment(sketch, "E91.MirrorCS", {"start": v(0, -74.25) * mm, "end": v(0, -104.25) * mm, "construction": true});
            skLineSegment(sketch, "E92.MirrorCS", {"start": v(-15, -92.25) * mm, "end": v(-33, -74.25) * mm});
            skLineSegment(sketch, "E93.MirrorCS", {"start": v(-15, -104.25) * mm, "end": v(-15, -92.25) * mm});
            skLineSegment(sketch, "E94", {"start": v(-33, 74.25) * mm, "end": v(-64.25, 74.25) * mm});
            skLineSegment(sketch, "E95", {"start": v(-74.25, 64.25) * mm, "end": v(-74.25, 0) * mm});
            skLineSegment(sketch, "E96", {"start": v(-74.25, 0) * mm, "end": v(-74.25, -64.25) * mm});
            skLineSegment(sketch, "E97", {"start": v(33, 74.25) * mm, "end": v(64.25, 74.25) * mm});
            skLineSegment(sketch, "E98", {"start": v(74.25, 64.25) * mm, "end": v(74.25, -64.25) * mm});
            skLineSegment(sketch, "E99", {"start": v(-33, -74.25) * mm, "end": v(-64.25, -74.25) * mm});
            skLineSegment(sketch, "E100", {"start": v(33, -74.25) * mm, "end": v(64.25, -74.25) * mm});
            skArc(sketch, "E101", {"start": v(64.25, -74.25) * mm, "mid": v(71.32, -71.32) * mm, "end": v(74.25, -64.25) * mm});
            skArc(sketch, "E102", {"start": v(-74.25, -64.25) * mm, "mid": v(-71.32, -71.32) * mm, "end": v(-64.25, -74.25) * mm});
            skArc(sketch, "E103", {"start": v(74.25, 64.25) * mm, "mid": v(71.32, 71.32) * mm, "end": v(64.25, 74.25) * mm});
            skArc(sketch, "E104", {"start": v(-64.25, 74.25) * mm, "mid": v(-71.32, 71.32) * mm, "end": v(-74.25, 64.25) * mm});
            skCircle(sketch, "E105", {"center": v(-60, -60) * mm, "radius": 4 * mm});
            skCircle(sketch, "E106", {"center": v(60, -60) * mm, "radius": 4 * mm});
            skCircle(sketch, "E107", {"center": v(60, 60) * mm, "radius": 4 * mm});
            skCircle(sketch, "E108", {"center": v(-60, 60) * mm, "radius": 4 * mm});
            skLineSegment(sketch, "E109", {"start": v(-60, 38.83) * mm, "end": v(-60, -38.83) * mm});
            skLineSegment(sketch, "E110", {"start": v(60, -38.83) * mm, "end": v(60, 38.83) * mm});
            skArc(sketch, "E111", {"start": v(60, 38.83) * mm, "mid": v(58.44, 44.2) * mm, "end": v(54.26, 47.88) * mm});
            skArc(sketch, "E112", {"start": v(-54.26, 47.88) * mm, "mid": v(-58.44, 44.2) * mm, "end": v(-60, 38.83) * mm});
            skArc(sketch, "E113", {"start": v(54.26, 47.88) * mm, "mid": v(0, 59.74) * mm, "end": v(-54.26, 47.88) * mm});
            skArc(sketch, "E114", {"start": v(-60, -38.83) * mm, "mid": v(-58.44, -44.2) * mm, "end": v(-54.26, -47.88) * mm});
            skArc(sketch, "E115", {"start": v(54.26, -47.88) * mm, "mid": v(58.44, -44.2) * mm, "end": v(60, -38.83) * mm});
            skArc(sketch, "E116", {"start": v(-54.26, -47.88) * mm, "mid": v(0, -59.74) * mm, "end": v(54.26, -47.88) * mm});
            skSolve(sketch);
        }
        {
            var Q0;
            Q0 = qSketchRegion(id + "F16", true);
            extrude(context, id + "F17", {"entities" : qUnion([Q0]), "depth" : 5 * mm});
        }
    });
